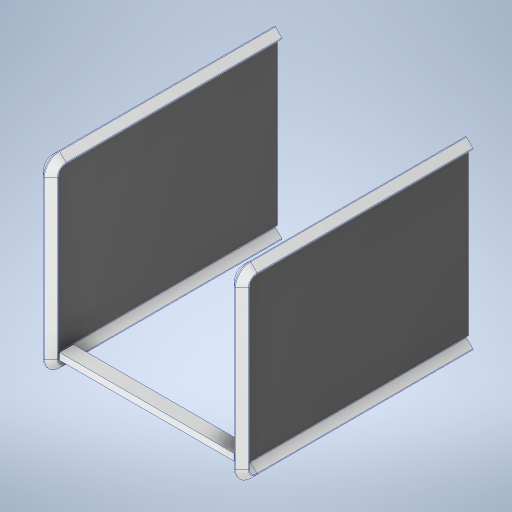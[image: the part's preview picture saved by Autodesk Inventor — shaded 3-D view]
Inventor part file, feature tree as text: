
AUTODESK INVENTOR PART (.ipt)
format: ipt  version: 2024 (Build 280153000, 153)  size: 376,832 bytes
history: native  units: mm
features: sketch x5, mirror x4, extrude x3, projected_geometry x3, plane x1, sweep x1, other x1
ambient origin geometry x8: Origin, YZ Plane, XZ Plane, XY Plane, X Axis, Y Axis, Z Axis, Center Point
bodies: Solid1 (feature_tree), Solid3 (feature_tree)
feature tree (18):
  extrude  "Extrusion1"  Depth=553.0mm
  mirror  "Mirror1"
  mirror  "Mirror2"
  plane  "Work Plane1"
  sweep  "Sweep1"
  mirror  "Mirror3"
  extrude  "Extrusion2"  TaperAngle=90.0deg  [1 undecoded]
  mirror  "Mirror4"
  extrude  "Extrusion3"  TaperAngle=0.0deg  [1 undecoded]
  sketch  "Sketch1"  dims[d0=553.0mm d1=503.0mm]
  sketch  "Sketch2"  dims[d2=30.0mm d3=2.0mm]
  sketch  "Sketch3"  dims[d4=625.0mm d5=0.0mm d6=90.0deg]
  projected_geometry  "Projected Loop1"
  sketch  "Sketch4"  dims[d8=455.0mm d9=0.0mm d10=0.0mm]
  other  "Side Panels"
  sketch  "Sketch5"  dims[d11=460.0mm d12=1.115224mm d13=6.35mm d14=3.0mm d15=0.0mm d16=20.0mm d17=40.0mm d18=40.0mm d19=20.0mm d20=1.5mm d21=1.5mm d22=2.5mm d23=20.0mm d24=40.0mm d25=40.0mm d26=20.0mm d27=505.0mm d28=0.0mm]
  projected_geometry  "Project Cut Edges1"
  projected_geometry  "Project Cut Edges2"
note: 2 required parameter values undecoded (feature->parameter linkage not recoverable at this tier; creation-order binding heuristic only, values carry confidence <= 0.55)
